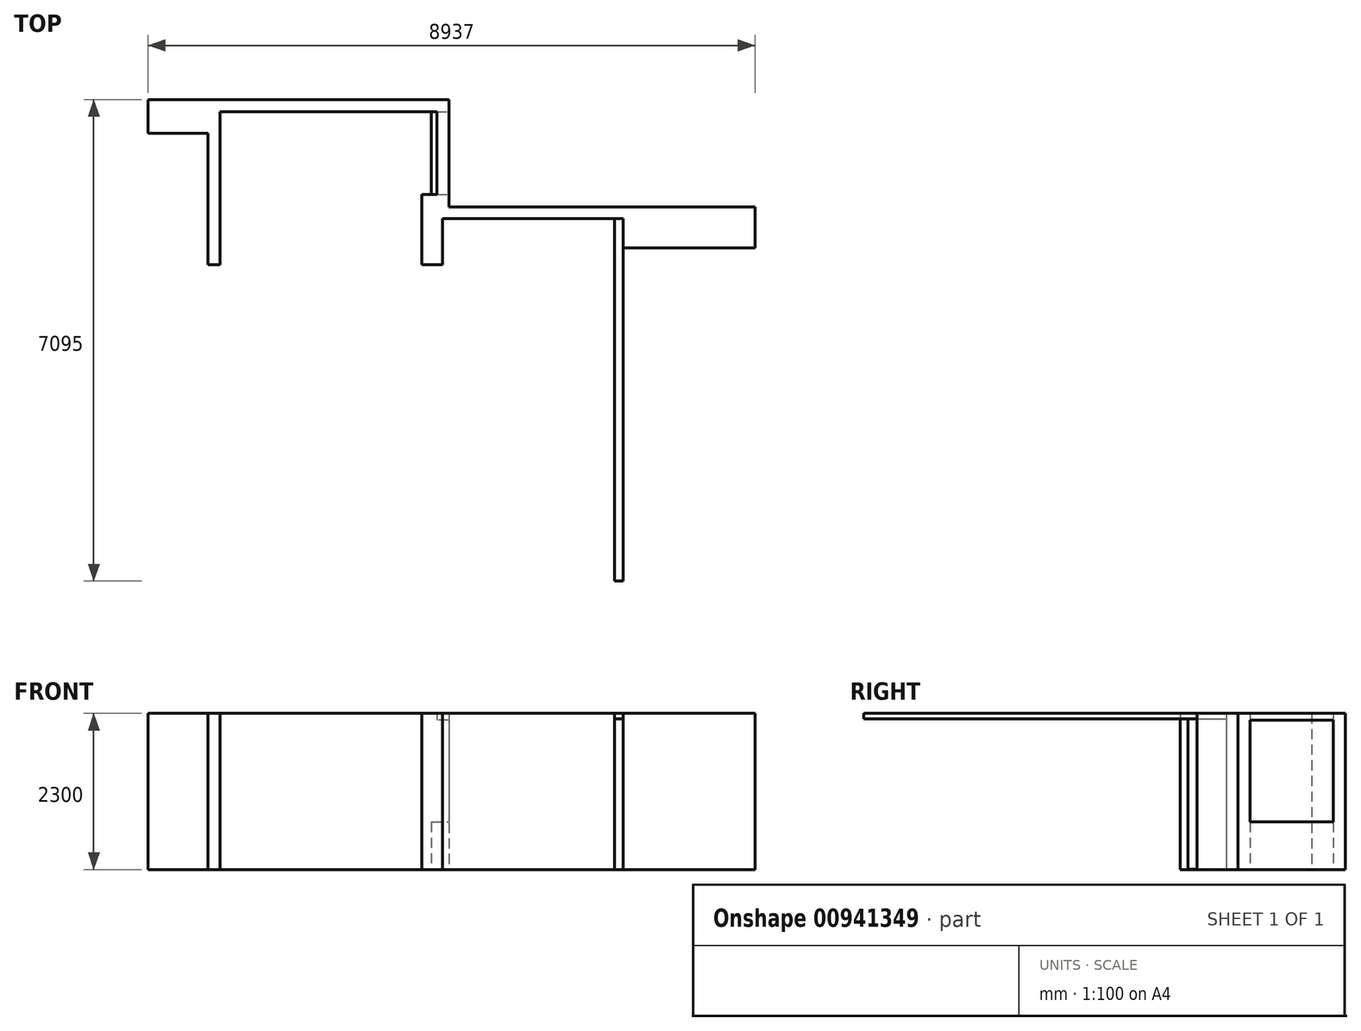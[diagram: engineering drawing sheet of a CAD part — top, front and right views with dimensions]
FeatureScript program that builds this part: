
annotation { "Feature Type Name" : "Feature", "Feature Type Description" : "" }
export const myFeature = defineFeature(function(context is Context, id is Id, definition is map)
    precondition{}
    {
        {
            var Q0;
            Q0=qCreatedBy(makeId("Top.planeOp"),FACE);
            var sketch = newSketch(context, id + "F0", { "sketchPlane" : qUnion([Q0])});
            skLineSegment(sketch, "E0", {"start": v(-307, 355) * mm, "end": v(-307, -680) * mm});
            skLineSegment(sketch, "E1", {"start": v(-307, -680) * mm, "end": v(0, -680) * mm});
            skLineSegment(sketch, "E2", {"start": v(0, -680) * mm, "end": v(0, 0) * mm});
            skLineSegment(sketch, "E3", {"start": v(0, 0) * mm, "end": v(2660, 0) * mm});
            skLineSegment(sketch, "E4", {"start": v(2660, 0) * mm, "end": v(2660, -430) * mm});
            skLineSegment(sketch, "E5", {"start": v(2660, -430) * mm, "end": v(4600, -430) * mm});
            skLineSegment(sketch, "E6", {"start": v(4600, -430) * mm, "end": v(4600, 175) * mm});
            skLineSegment(sketch, "E7", {"start": v(93, 1755) * mm, "end": v(-4337, 1755) * mm});
            skLineSegment(sketch, "E8", {"start": v(-307, 355) * mm, "end": v(-87, 355) * mm});
            skLineSegment(sketch, "E9", {"start": v(-87, 355) * mm, "end": v(-87, 1575) * mm});
            skLineSegment(sketch, "E10", {"start": v(-87, 1575) * mm, "end": v(-3277, 1575) * mm});
            skLineSegment(sketch, "E11", {"start": v(-3277, 1575) * mm, "end": v(-3277, -679) * mm});
            skLineSegment(sketch, "E12", {"start": v(-3277, -679) * mm, "end": v(-3457, -679) * mm});
            skLineSegment(sketch, "E13", {"start": v(-3457, -679) * mm, "end": v(-3457, 1261) * mm});
            skLineSegment(sketch, "E14", {"start": v(4600, 175) * mm, "end": v(93, 175) * mm});
            skLineSegment(sketch, "E15", {"start": v(93, 175) * mm, "end": v(93, 1755) * mm});
            skLineSegment(sketch, "E16", {"start": v(-4337, 1755) * mm, "end": v(-4337, 1261) * mm});
            skLineSegment(sketch, "E17", {"start": v(-3457, 1261) * mm, "end": v(-4337, 1261) * mm});
            skSolve(sketch);
        }
        {
            var Q0;
            Q0=makeQuery(id+"F0.imprint","IMPRINT",FACE,{"disambiguationData":[TD([[makeQuery(id+"F0.imprint","IMPRINT",EDGE,{"derivedFrom":sQuery(id+"F0.wireOp",EDGE,"E0")}),1.0]])]});
            extrude(context, id + "F1", {"entities" : qUnion([Q0]), "depth" : 2300 * mm, "offsetDistance" : 25 * mm});
        }
        {
            var Q0;
            Q0=makeQuery(id+"F1.opExtrude","SWEPT_FACE",FACE,{"disambiguationData":[OSD([sQuery(id+"F0.wireOp",EDGE,"E9")])]});
            var sketch = newSketch(context, id + "F2", { "sketchPlane" : qUnion([Q0])});
            skLineSegment(sketch, "E18.bottom", {"start": v(-1575, 0) * mm, "end": v(-355, 0) * mm});
            skLineSegment(sketch, "E18.top", {"start": v(-1575, 700) * mm, "end": v(-355, 700) * mm});
            skLineSegment(sketch, "E18.left", {"start": v(-1575, 0) * mm, "end": v(-1575, 700) * mm});
            skLineSegment(sketch, "E18.right", {"start": v(-355, 0) * mm, "end": v(-355, 700) * mm});
            skLineSegment(sketch, "E19.bottom", {"start": v(-1575, 2200) * mm, "end": v(-355, 2200) * mm});
            skLineSegment(sketch, "E19.left", {"start": v(-1575, 2200) * mm, "end": v(-1575, 700) * mm});
            skLineSegment(sketch, "E19.right", {"start": v(-355, 2200) * mm, "end": v(-355, 700) * mm});
            skSolve(sketch);
        }
        {
            var Q0;
            Q0=makeQuery(id+"F2.imprint","IMPRINT",FACE,{"disambiguationData":[TD([[makeQuery(id+"F2.imprint","IMPRINT",EDGE,{"derivedFrom":sQuery(id+"F2.wireOp",EDGE,"E18.bottom")}),-1.0]])]});
            extrude(context, id + "F3", {"entities" : qUnion([Q0]), "operationType" : NewBodyOperationType.ADD, "depth" : 80 * mm, "offsetDistance" : 25 * mm});
        }
        {
            var Q0;
            Q0=makeQuery(id+"F2.imprint","IMPRINT",FACE,{"disambiguationData":[TD([[makeQuery(id+"F2.imprint","IMPRINT",EDGE,{"derivedFrom":sQuery(id+"F2.wireOp",EDGE,"E19.bottom")}),-1.0]])]});
            extrude(context, id + "F4", {"entities" : qUnion([Q0]), "operationType" : NewBodyOperationType.REMOVE, "endBound" : BoundingType.THROUGH_ALL, "oppositeDirection" : true, "depth" : 25 * mm, "offsetDistance" : 25 * mm});
        }
        {
            var Q0;
            Q0=makeQuery(id+"F1.opExtrude","SWEPT_FACE",FACE,{"disambiguationData":[OSD([sQuery(id+"F0.wireOp",EDGE,"E3")])]});
            var sketch = newSketch(context, id + "F5", { "sketchPlane" : qUnion([Q0])});
            skLineSegment(sketch, "E20.bottom", {"start": v(2660, 2300) * mm, "end": v(2530, 2300) * mm});
            skLineSegment(sketch, "E20.top", {"start": v(2660, 2220) * mm, "end": v(2530, 2220) * mm});
            skLineSegment(sketch, "E20.left", {"start": v(2660, 2300) * mm, "end": v(2660, 2220) * mm});
            skLineSegment(sketch, "E20.right", {"start": v(2530, 2300) * mm, "end": v(2530, 2220) * mm});
            skLineSegment(sketch, "E21.bottom", {"start": v(2534, 2220) * mm, "end": v(2534.5, 2220) * mm});
            skLineSegment(sketch, "E21.top", {"start": v(2534, 5) * mm, "end": v(2534.5, 5) * mm});
            skLineSegment(sketch, "E21.left", {"start": v(2534, 2220) * mm, "end": v(2534, 5) * mm});
            skLineSegment(sketch, "E21.right", {"start": v(2534.5, 2220) * mm, "end": v(2534.5, 5) * mm});
            skSolve(sketch);
        }
        {
            var Q0;
            Q0=makeQuery(id+"F5.imprint","IMPRINT",FACE,{"disambiguationData":[TD([[makeQuery(id+"F5.imprint","IMPRINT",EDGE,{"derivedFrom":sQuery(id+"F5.wireOp",EDGE,"E20.bottom")}),-1.0]])]});
            extrude(context, id + "F6", {"entities" : qUnion([Q0]), "depth" : 5340 * mm, "offsetDistance" : 25 * mm});
        }
        {
            var Q0;
            Q0=makeQuery(id+"F5.imprint","IMPRINT",FACE,{"disambiguationData":[TD([[makeQuery(id+"F5.imprint","IMPRINT",EDGE,{"derivedFrom":sQuery(id+"F5.wireOp",EDGE,"E21.top")}),1.0]])]});
            extrude(context, id + "F7", {"entities" : qUnion([Q0]), "depth" : 560 * mm, "offsetDistance" : 25 * mm});
        }
    });
